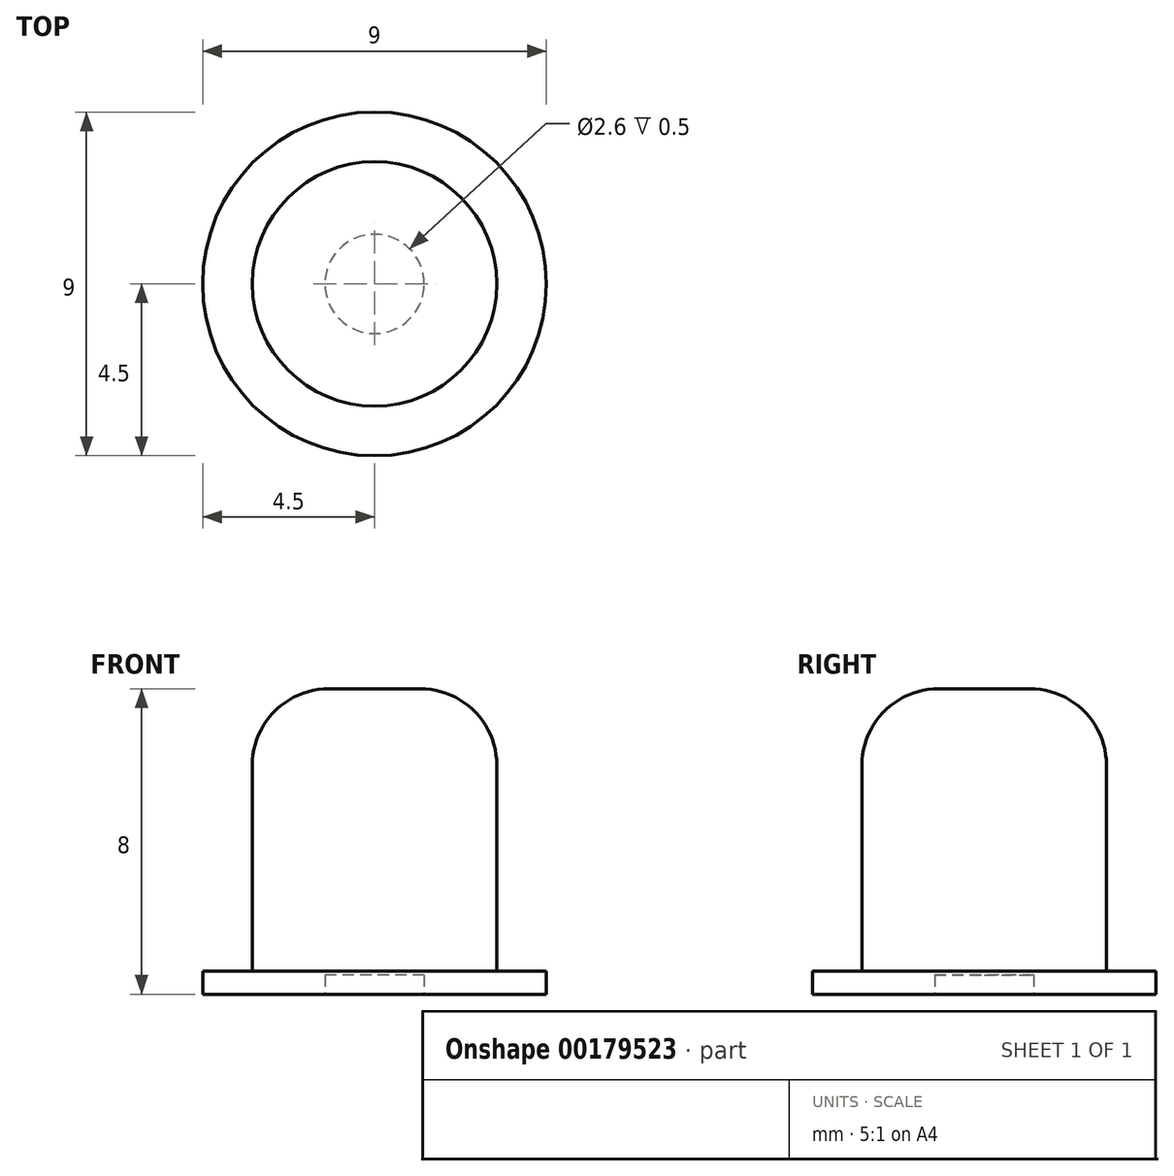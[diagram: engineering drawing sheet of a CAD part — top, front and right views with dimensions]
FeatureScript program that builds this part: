
annotation { "Feature Type Name" : "Feature", "Feature Type Description" : "" }
export const myFeature = defineFeature(function(context is Context, id is Id, definition is map)
    precondition{}
    {
        {
            var Q0;
            Q0=qCreatedBy(makeId("Top.planeOp"),FACE);
            var sketch = newSketch(context, id + "F0", { "sketchPlane" : qUnion([Q0])});
            skCircle(sketch, "E0", {"center": v(0, 0) * mm, "radius": 3.2 * mm});
            skCircle(sketch, "E1", {"center": v(0, 0) * mm, "radius": 4.5 * mm});
            skCircle(sketch, "E2", {"center": v(0, 0) * mm, "radius": 1.3 * mm});
            skSolve(sketch);
        }
        {
            var Q0;
            Q0=makeQuery(id+"F0.imprint","IMPRINT",FACE,{"disambiguationData":[TD([[makeQuery(id+"F0.imprint","IMPRINT",EDGE,{"derivedFrom":sQuery(id+"F0.wireOp",EDGE,"E0")}),-1.0]])]});
            var Q1;
            Q1=makeQuery(id+"F0.imprint","IMPRINT",FACE,{"disambiguationData":[TD([[makeQuery(id+"F0.imprint","IMPRINT",EDGE,{"derivedFrom":sQuery(id+"F0.wireOp",EDGE,"E0")}),1.0]])]});
            extrude(context, id + "F1", {"entities" : qUnion([Q0, Q1]), "depth" : 0.6 * mm});
        }
        {
            var Q0;
            Q0=makeQuery(id+"F0.imprint","IMPRINT",FACE,{"disambiguationData":[TD([[makeQuery(id+"F0.imprint","IMPRINT",EDGE,{"derivedFrom":sQuery(id+"F0.wireOp",EDGE,"E0")}),1.0]])]});
            var Q1;
            Q1=makeQuery(id+"F0.imprint","IMPRINT",FACE,{"disambiguationData":[TD([[makeQuery(id+"F0.imprint","IMPRINT",EDGE,{"derivedFrom":sQuery(id+"F0.wireOp",EDGE,"E2")}),1.0]])]});
            extrude(context, id + "F2", {"entities" : qUnion([Q0, Q1]), "operationType" : NewBodyOperationType.ADD, "depth" : 8 * mm});
        }
        {
            var Q0;
            Q0=makeQuery(id+"F2.opExtrude","CAP_EDGE",EDGE,{"disambiguationData":[OSD([sQuery(id+"F0.wireOp",EDGE,"E0")])],"isStart":false});
            fillet(context, id + "F3", {"entities" : qUnion([Q0]), "radius" : 2 * mm, "tangentPropagation" : true, "allowEdgeOverflow" : false});
        }
        {
            var Q0;
            Q0=makeQuery(id+"F0.imprint","IMPRINT",FACE,{"disambiguationData":[TD([[makeQuery(id+"F0.imprint","IMPRINT",EDGE,{"derivedFrom":sQuery(id+"F0.wireOp",EDGE,"E2")}),1.0]])]});
            extrude(context, id + "F4", {"entities" : qUnion([Q0]), "operationType" : NewBodyOperationType.REMOVE, "depth" : 0.5 * mm});
        }
    });
